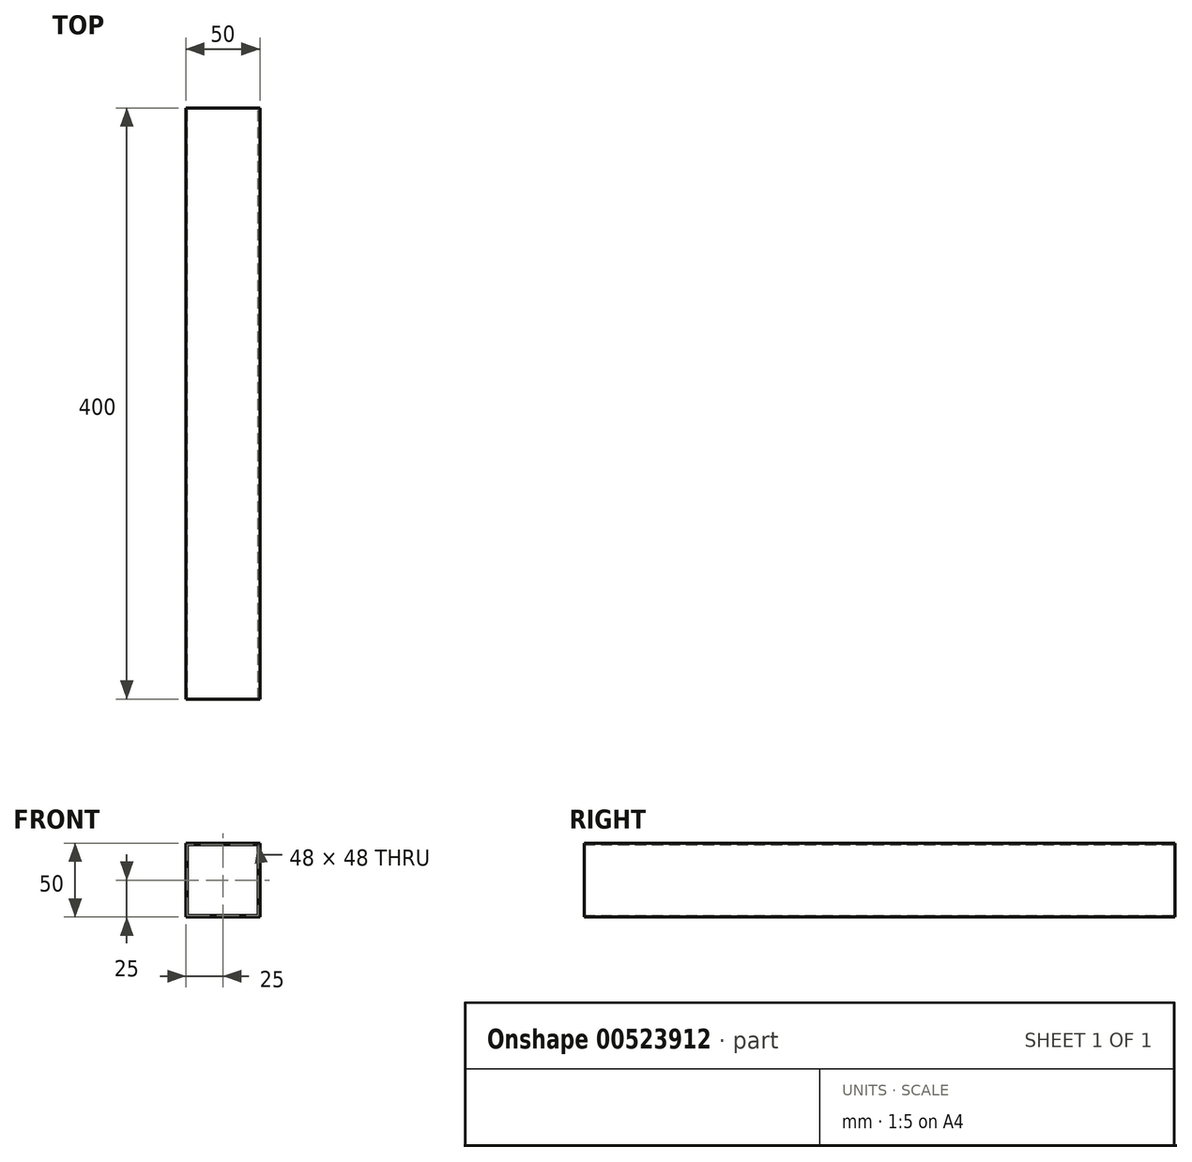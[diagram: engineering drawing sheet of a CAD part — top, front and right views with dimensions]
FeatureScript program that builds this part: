
annotation { "Feature Type Name" : "Feature", "Feature Type Description" : "" }
export const myFeature = defineFeature(function(context is Context, id is Id, definition is map)
    precondition{}
    {
        {
            var Q0;
            Q0=qCreatedBy(makeId("Front.planeOp"),FACE);
            var sketch = newSketch(context, id + "F0", { "sketchPlane" : qUnion([Q0])});
            skLineSegment(sketch, "E0.bottom", {"start": v(25, 25) * mm, "end": v(-25, 25) * mm});
            skLineSegment(sketch, "E0.top", {"start": v(25, -25) * mm, "end": v(-25, -25) * mm});
            skLineSegment(sketch, "E0.left", {"start": v(25, 25) * mm, "end": v(25, -25) * mm});
            skLineSegment(sketch, "E0.right", {"start": v(-25, 25) * mm, "end": v(-25, -25) * mm});
            skPoint(sketch, "E0.middle", {"position": v(0, 0) * mm});
            skLineSegment(sketch, "E1.bottom", {"start": v(24, 24) * mm, "end": v(-24, 24) * mm});
            skLineSegment(sketch, "E1.top", {"start": v(24, -24) * mm, "end": v(-24, -24) * mm});
            skLineSegment(sketch, "E1.left", {"start": v(24, 24) * mm, "end": v(24, -24) * mm});
            skLineSegment(sketch, "E1.right", {"start": v(-24, 24) * mm, "end": v(-24, -24) * mm});
            skSolve(sketch);
        }
        {
            var Q0;
            Q0=makeQuery(id+"F0.imprint","IMPRINT",FACE,{"disambiguationData":[TD([[makeQuery(id+"F0.imprint","IMPRINT",EDGE,{"derivedFrom":sQuery(id+"F0.wireOp",EDGE,"E0.bottom")}),1.0]])]});
            extrude(context, id + "F1", {"entities" : qUnion([Q0]), "depth" : 400 * mm, "offsetDistance" : 25 * mm});
        }
    });
